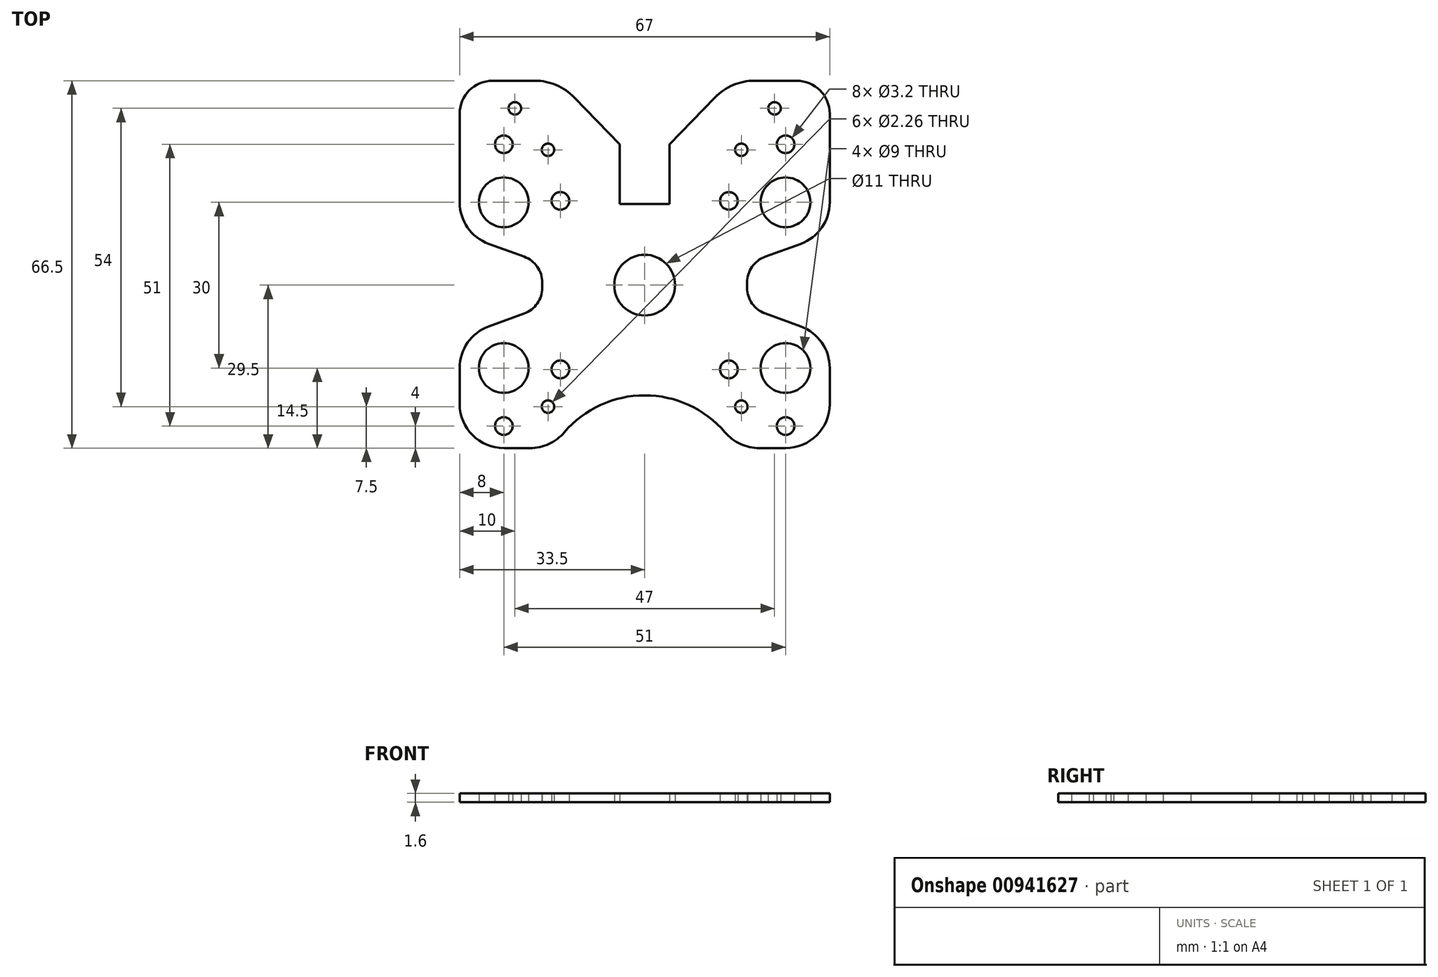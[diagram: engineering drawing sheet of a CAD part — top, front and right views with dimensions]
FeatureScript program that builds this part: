
annotation { "Feature Type Name" : "Feature", "Feature Type Description" : "" }
export const myFeature = defineFeature(function(context is Context, id is Id, definition is map)
    precondition{}
    {
        {
            var Q0;
            Q0=qCreatedBy(makeId("Top.planeOp"),FACE);
            var sketch = newSketch(context, id + "F0", { "sketchPlane" : qUnion([Q0])});
            skLineSegment(sketch, "E0.bottom", {"start": v(15.25, 7.25) * mm, "end": v(-15.25, 7.25) * mm, "construction": true});
            skLineSegment(sketch, "E0.top", {"start": v(15.25, -23.25) * mm, "end": v(-15.25, -23.25) * mm, "construction": true});
            skLineSegment(sketch, "E0.left", {"start": v(15.25, 7.25) * mm, "end": v(15.25, -23.25) * mm, "construction": true});
            skLineSegment(sketch, "E0.right", {"start": v(-15.25, 7.25) * mm, "end": v(-15.25, -23.25) * mm, "construction": true});
            skPoint(sketch, "E0.middle", {"position": v(0, -8) * mm});
            skLineSegment(sketch, "E1.bottom", {"start": v(25.5, 17.5) * mm, "end": v(-25.5, 17.5) * mm, "construction": true});
            skLineSegment(sketch, "E1.top", {"start": v(25.5, -33.5) * mm, "end": v(-25.5, -33.5) * mm, "construction": true});
            skLineSegment(sketch, "E1.left", {"start": v(25.5, 17.5) * mm, "end": v(25.5, -33.5) * mm, "construction": true});
            skLineSegment(sketch, "E1.right", {"start": v(-25.5, 17.5) * mm, "end": v(-25.5, -33.5) * mm, "construction": true});
            skCircle(sketch, "E2", {"center": v(-25.5, 17.5) * mm, "radius": 1.6 * mm});
            skCircle(sketch, "E3", {"center": v(25.5, 17.5) * mm, "radius": 1.6 * mm});
            skCircle(sketch, "E4", {"center": v(-25.5, -33.5) * mm, "radius": 1.6 * mm});
            skCircle(sketch, "E5", {"center": v(25.5, -33.5) * mm, "radius": 1.6 * mm});
            skCircle(sketch, "E6", {"center": v(-15.25, -23.25) * mm, "radius": 1.6 * mm});
            skCircle(sketch, "E7", {"center": v(15.25, -23.25) * mm, "radius": 1.6 * mm});
            skCircle(sketch, "E8", {"center": v(-15.25, 7.25) * mm, "radius": 1.6 * mm});
            skCircle(sketch, "E9", {"center": v(15.25, 7.25) * mm, "radius": 1.6 * mm});
            skLineSegment(sketch, "E10", {"start": v(-4.5, 6.68) * mm, "end": v(-4.5, 17.5) * mm});
            skLineSegment(sketch, "E11", {"start": v(-4.5, 17.5) * mm, "end": v(-10.72, 23.9) * mm});
            skLineSegment(sketch, "E12", {"start": v(-4.5, 6.68) * mm, "end": v(0, 6.68) * mm});
            skCircle(sketch, "E13", {"center": v(-23.5, 24) * mm, "radius": 1.13 * mm});
            skPoint(sketch, "E13.first.point", {"position": v(-24.6, 24.3) * mm});
            skPoint(sketch, "E13.second.point", {"position": v(-22.4, 24.3) * mm});
            skPoint(sketch, "E13.third.point", {"position": v(-23.5, 22.87) * mm});
            skCircle(sketch, "E14", {"center": v(-17.5, 16.5) * mm, "radius": 1.13 * mm});
            skPoint(sketch, "E14.first.point", {"position": v(-18.63, 16.5) * mm});
            skPoint(sketch, "E14.second.point", {"position": v(-17.2, 17.6) * mm});
            skPoint(sketch, "E14.third.point", {"position": v(-16.52, 15.93) * mm});
            skCircle(sketch, "E15", {"center": v(-17.5, -30) * mm, "radius": 1.13 * mm});
            skPoint(sketch, "E15.first.point", {"position": v(-18.63, -30) * mm});
            skPoint(sketch, "E15.second.point", {"position": v(-16.7, -30.8) * mm});
            skPoint(sketch, "E15.third.point", {"position": v(-16.93, -29.02) * mm});
            skLineSegment(sketch, "E16.bottom", {"start": v(-25.5, 7) * mm, "end": v(25.5, 7) * mm, "construction": true});
            skLineSegment(sketch, "E16.top", {"start": v(-25.5, -23) * mm, "end": v(25.5, -23) * mm, "construction": true});
            skLineSegment(sketch, "E16.left", {"start": v(-25.5, 7) * mm, "end": v(-25.5, -23) * mm, "construction": true});
            skLineSegment(sketch, "E16.right", {"start": v(25.5, 7) * mm, "end": v(25.5, -23) * mm, "construction": true});
            skCircle(sketch, "E17", {"center": v(-25.5, 7) * mm, "radius": 4.5 * mm});
            skCircle(sketch, "E18", {"center": v(-25.5, -23) * mm, "radius": 4.5 * mm});
            skCircle(sketch, "E19.MirrorC", {"center": v(25.5, 7) * mm, "radius": 4.5 * mm});
            skCircle(sketch, "E20.MirrorC", {"center": v(25.5, -23) * mm, "radius": 4.5 * mm});
            skCircle(sketch, "E21.MirrorC", {"center": v(17.5, -30) * mm, "radius": 1.13 * mm});
            skCircle(sketch, "E22.MirrorC", {"center": v(17.5, 16.5) * mm, "radius": 1.13 * mm});
            skCircle(sketch, "E23.MirrorC", {"center": v(23.5, 24) * mm, "radius": 1.13 * mm});
            skLineSegment(sketch, "E24", {"start": v(-25.5, 0) * mm, "end": v(-25.5, -16) * mm, "construction": true});
            skLineSegment(sketch, "E25", {"start": v(0, -8) * mm, "end": v(-33.11, -8) * mm, "construction": true});
            skCircle(sketch, "E26", {"center": v(0, -8) * mm, "radius": 5.5 * mm});
            skPoint(sketch, "E27", {"position": v(0, -23.25) * mm});
            skLineSegment(sketch, "E28", {"start": v(-25.5, 7) * mm, "end": v(-28.23, 14.5) * mm, "construction": true});
            skLineSegment(sketch, "E29", {"start": v(-10.72, 23.9) * mm, "end": v(-12.71, 25.96) * mm});
            skLineSegment(sketch, "E30", {"start": v(-19.89, 29) * mm, "end": v(-27.5, 29) * mm});
            skLineSegment(sketch, "E31", {"start": v(-33.5, 23) * mm, "end": v(-33.5, 7) * mm});
            skPoint(sketch, "E32.visualSharp", {"position": v(-33.5, 29) * mm});
            skArc(sketch, "E32.filletArc", {"start": v(-27.5, 29) * mm, "mid": v(-31.74, 27.24) * mm, "end": v(-33.5, 23) * mm});
            skPoint(sketch, "E33.visualSharp", {"position": v(-15.66, 29) * mm});
            skArc(sketch, "E33.filletArc", {"start": v(-12.71, 25.96) * mm, "mid": v(-16, 28.2) * mm, "end": v(-19.89, 29) * mm});
            skArc(sketch, "E34", {"start": v(-33.5, 7) * mm, "mid": v(-32.05, 2.41) * mm, "end": v(-28.24, -0.52) * mm});
            skLineSegment(sketch, "E35", {"start": v(-28.24, -0.52) * mm, "end": v(-21.82, -2.85) * mm});
            skLineSegment(sketch, "E36", {"start": v(-18.53, -7.55) * mm, "end": v(-18.53, -8) * mm});
            skLineSegment(sketch, "E37", {"start": v(-25.5, 7) * mm, "end": v(-28.24, -0.52) * mm, "construction": true});
            skPoint(sketch, "E38.visualSharp", {"position": v(-18.53, -4.05) * mm});
            skArc(sketch, "E38.filletArc", {"start": v(-18.53, -7.55) * mm, "mid": v(-19.44, -4.68) * mm, "end": v(-21.82, -2.85) * mm});
            skLineSegment(sketch, "E39.MirrorCS", {"start": v(-28.24, -15.48) * mm, "end": v(-21.82, -13.15) * mm});
            skLineSegment(sketch, "E40.MirrorCS", {"start": v(-18.53, -8.45) * mm, "end": v(-18.53, -8) * mm});
            skArc(sketch, "E41.MirrorCS", {"start": v(-18.53, -8.45) * mm, "mid": v(-19.44, -11.32) * mm, "end": v(-21.82, -13.15) * mm});
            skArc(sketch, "E42.MirrorCS", {"start": v(-33.5, -23) * mm, "mid": v(-32.05, -18.41) * mm, "end": v(-28.24, -15.48) * mm});
            skLineSegment(sketch, "E43", {"start": v(-33.5, -23) * mm, "end": v(-33.5, -29.5) * mm});
            skArc(sketch, "E44", {"start": v(-33.5, -29.5) * mm, "mid": v(-31.16, -35.16) * mm, "end": v(-25.5, -37.5) * mm});
            skLineSegment(sketch, "E45", {"start": v(-25.5, -37.5) * mm, "end": v(-20.78, -37.5) * mm});
            skArc(sketch, "E46", {"start": v(-20.78, -37.5) * mm, "mid": v(-17.34, -36.75) * mm, "end": v(-14.53, -34.63) * mm});
            skArc(sketch, "E47", {"start": v(-14.53, -34.63) * mm, "mid": v(-8, -29.7) * mm, "end": v(0, -27.95) * mm});
            skLineSegment(sketch, "E48", {"start": v(0, -27.95) * mm, "end": v(6.9, -27.95) * mm, "construction": true});
            skLineSegment(sketch, "E49.MirrorCS", {"start": v(4.5, 6.68) * mm, "end": v(0, 6.68) * mm});
            skLineSegment(sketch, "E50.MirrorCS", {"start": v(4.5, 6.68) * mm, "end": v(4.5, 17.5) * mm});
            skLineSegment(sketch, "E51.MirrorCS", {"start": v(4.5, 17.5) * mm, "end": v(10.72, 23.9) * mm});
            skLineSegment(sketch, "E52.MirrorCS", {"start": v(10.72, 23.9) * mm, "end": v(12.71, 25.96) * mm});
            skArc(sketch, "E53.MirrorCS", {"start": v(12.71, 25.96) * mm, "mid": v(16, 28.2) * mm, "end": v(19.89, 29) * mm});
            skLineSegment(sketch, "E54.MirrorCS", {"start": v(19.89, 29) * mm, "end": v(27.5, 29) * mm});
            skArc(sketch, "E55.MirrorCS", {"start": v(27.5, 29) * mm, "mid": v(31.74, 27.24) * mm, "end": v(33.5, 23) * mm});
            skLineSegment(sketch, "E56.MirrorCS", {"start": v(33.5, 23) * mm, "end": v(33.5, 7) * mm});
            skArc(sketch, "E57.MirrorCS", {"start": v(33.5, 7) * mm, "mid": v(32.05, 2.41) * mm, "end": v(28.24, -0.52) * mm});
            skLineSegment(sketch, "E58.MirrorCS", {"start": v(28.24, -0.52) * mm, "end": v(21.82, -2.85) * mm});
            skLineSegment(sketch, "E59.MirrorCS", {"start": v(18.53, -7.55) * mm, "end": v(18.53, -8) * mm});
            skLineSegment(sketch, "E60.MirrorCS", {"start": v(18.53, -8.45) * mm, "end": v(18.53, -8) * mm});
            skArc(sketch, "E61.MirrorCS", {"start": v(18.53, -7.55) * mm, "mid": v(19.44, -4.68) * mm, "end": v(21.82, -2.85) * mm});
            skArc(sketch, "E62.MirrorCS", {"start": v(18.53, -8.45) * mm, "mid": v(19.44, -11.32) * mm, "end": v(21.82, -13.15) * mm});
            skArc(sketch, "E63.MirrorCS", {"start": v(33.5, -23) * mm, "mid": v(32.05, -18.41) * mm, "end": v(28.24, -15.48) * mm});
            skLineSegment(sketch, "E64.MirrorCS", {"start": v(25.5, -37.5) * mm, "end": v(20.78, -37.5) * mm});
            skLineSegment(sketch, "E65.MirrorCS", {"start": v(33.5, -23) * mm, "end": v(33.5, -29.5) * mm});
            skArc(sketch, "E66.MirrorCS", {"start": v(33.5, -29.5) * mm, "mid": v(31.16, -35.16) * mm, "end": v(25.5, -37.5) * mm});
            skArc(sketch, "E67.MirrorCS", {"start": v(20.78, -37.5) * mm, "mid": v(17.34, -36.75) * mm, "end": v(14.53, -34.63) * mm});
            skArc(sketch, "E68.MirrorCS", {"start": v(14.53, -34.63) * mm, "mid": v(8, -29.7) * mm, "end": v(0, -27.95) * mm});
            skLineSegment(sketch, "E69", {"start": v(21.82, -13.15) * mm, "end": v(28.24, -15.48) * mm});
            skCircle(sketch, "E70", {"center": v(-25.5, 7) * mm, "radius": 7 * mm, "construction": true});
            skSolve(sketch);
        }
        {
            var Q0;
            Q0=makeQuery(id+"F0.imprint","IMPRINT",FACE,{"disambiguationData":[TD([[makeQuery(id+"F0.imprint","IMPRINT",EDGE,{"derivedFrom":sQuery(id+"F0.wireOp",EDGE,"E2")}),-1.0]])]});
            extrude(context, id + "F1", {"entities" : qUnion([Q0]), "depth" : 1.6 * mm, "offsetDistance" : 25 * mm});
        }
    });
